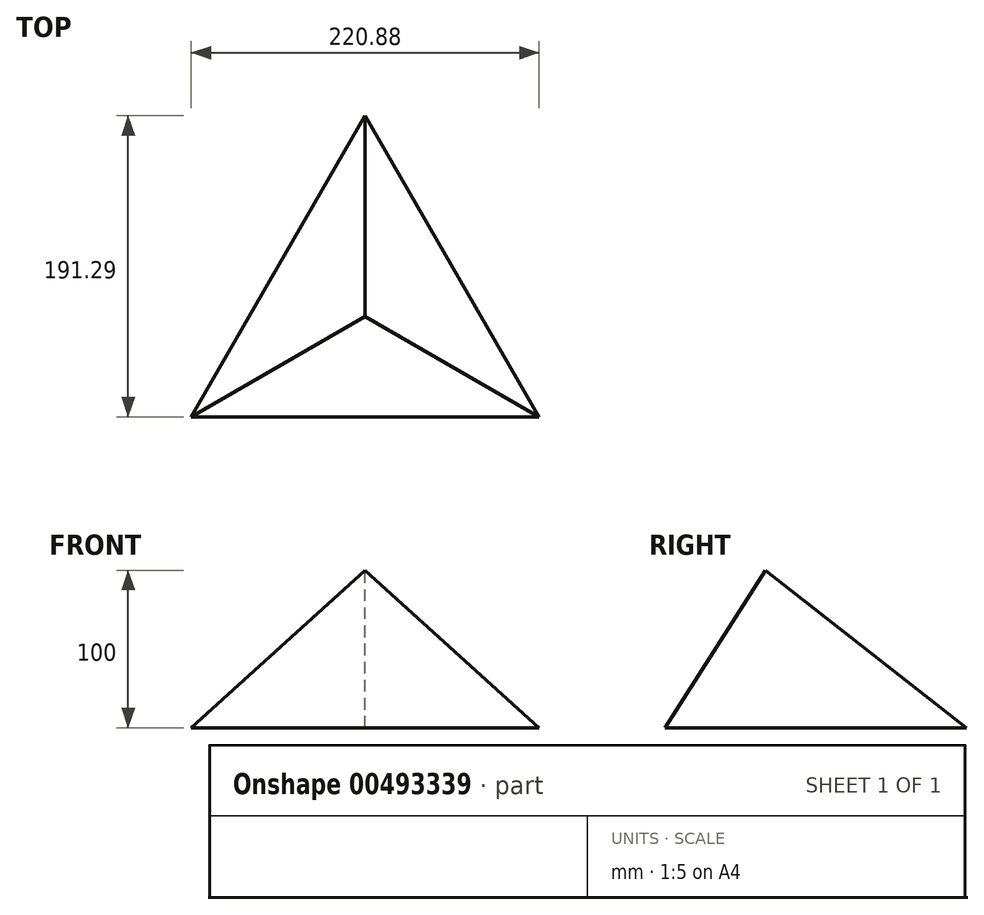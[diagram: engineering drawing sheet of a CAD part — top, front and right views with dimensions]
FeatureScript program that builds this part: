
annotation { "Feature Type Name" : "Feature", "Feature Type Description" : "" }
export const myFeature = defineFeature(function(context is Context, id is Id, definition is map)
    precondition{}
    {
        {
            var Q0;
            Q0=qCreatedBy(makeId("Top.planeOp"),FACE);
            var sketch = newSketch(context, id + "F0", { "sketchPlane" : qUnion([Q0])});
            skCircle(sketch, "E0.cCircle", {"center": v(0, 0) * mm, "radius": 127.53 * mm, "construction": true});
            skLineSegment(sketch, "E0.0", {"start": v(0, 127.53) * mm, "end": v(110.44, -63.76) * mm});
            skLineSegment(sketch, "E0.1", {"start": v(110.44, -63.76) * mm, "end": v(-110.44, -63.76) * mm});
            skLineSegment(sketch, "E0.2", {"start": v(-110.44, -63.76) * mm, "end": v(0, 127.53) * mm});
            skSolve(sketch);
        }
        {
            var Q0;
            Q0=qCreatedBy(makeId("Top.planeOp"),FACE);
            cPlane(context, id + "F1", {"entities" : qUnion([Q0]), "cplaneType" : CPlaneType.OFFSET, "offset" : 100 * mm, "width" : 150 * mm, "height" : 150 * mm});
        }
        {
            var Q0;
            Q0=qCreatedBy(id+"F1.planeOp",FACE);
            var sketch = newSketch(context, id + "F2", { "sketchPlane" : qUnion([Q0])});
            skPoint(sketch, "E1", {"position": v(0, 0) * mm});
            skSolve(sketch);
        }
        {
            var Q0;
            Q0=makeQuery(id+"F0.imprint","IMPRINT",FACE,{"disambiguationData":[TD([[makeQuery(id+"F0.imprint","IMPRINT",EDGE,{"derivedFrom":sQuery(id+"F0.wireOp",EDGE,"E0.0")}),-1.0]])]});
            var Q1;
            Q1=sQuery(id+"F2.wireOp",VERTEX,"E1");
            loft(context, id + "F3", {"sheetProfilesArray" : [{ "sheetProfileEntities" : qUnion([Q0]) }, { "sheetProfileEntities" : qUnion([Q1]) }]});
        }
    });
